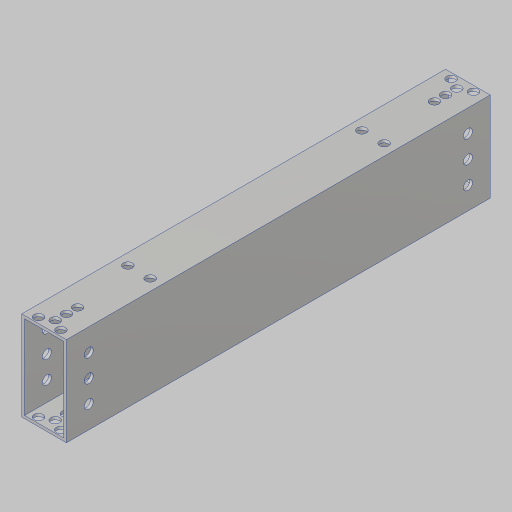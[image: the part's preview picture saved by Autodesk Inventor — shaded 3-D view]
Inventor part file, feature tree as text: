
AUTODESK INVENTOR PART (.ipt)
format: ipt  version: 2023.5 (Build 275446000, 446)  size: 184,832 bytes
history: native  units: in
note: dims shown in document units (in); Inventor stores cm internally (conversion verified against a paired STEP export)
features: hole x3, sketch x3, extrude x1, mirror x1, projected_geometry x1
ambient origin geometry x8: Origin, YZ Plane, XZ Plane, XY Plane, X Axis, Y Axis, Z Axis, Center Point
bodies: Solid1 (feature_tree)
feature tree (9):
  extrude  "Extrusion1"  Depth=0.5in
  hole  "Hole1"  [1 undecoded]
  hole  "Hole2"  [1 undecoded]
  hole  "Hole3"  [1 undecoded]
  mirror  "Mirror1"
  sketch  "Sketch2"  dims[d4=0.0in d5=0.5in]
  sketch  "Sketch3"  dims[d6=0.5in d7=0.5in]
  sketch  "Sketch4"  dims[d8=0.5in d9=0.5in d10=0.5in d11=0.201in d12=0.75in d13=0.385in d14=0.25in d15=0.5635in d16=1.0in d17=0.8108in d18=0.25in d19=0.25in d20=0.25in d21=0.5in d22=0.25in d23=0.25in d24=0.25in d25=0.201in d26=0.75in d27=0.385in d28=0.25in d29=0.5635in d30=1.0in d31=0.8108in d32=0.5in d33=2.0in d34=1.125in d35=0.201in d36=0.38in d37=0.385in d38=0.25in d39=0.5635in d40=1.0in d41=0.8108in]
  projected_geometry  "Project Cut Edges1"
note: 3 required parameter values undecoded (feature->parameter linkage not recoverable at this tier; creation-order binding heuristic only, values carry confidence <= 0.55)
